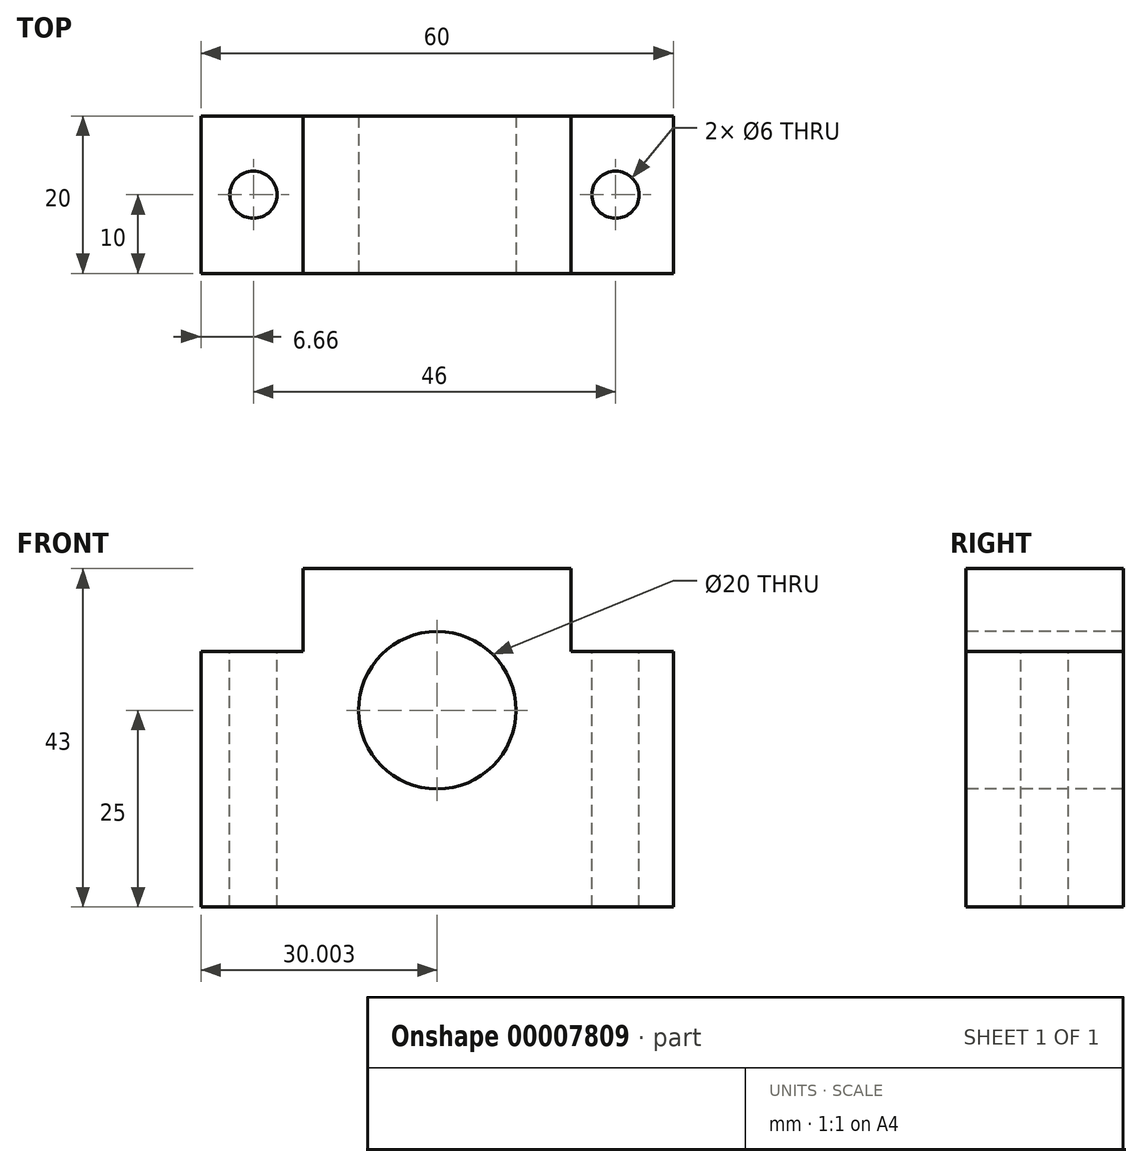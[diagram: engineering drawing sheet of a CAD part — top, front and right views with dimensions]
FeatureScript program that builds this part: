
annotation { "Feature Type Name" : "Feature", "Feature Type Description" : "" }
export const myFeature = defineFeature(function(context is Context, id is Id, definition is map)
    precondition{}
    {
        {
            var Q0;
            Q0=qCreatedBy(makeId("Front.planeOp"),FACE);
            var sketch = newSketch(context, id + "F0", { "sketchPlane" : qUnion([Q0])});
            skLineSegment(sketch, "E0.bottom", {"start": v(-29.66, 0) * mm, "end": v(30.34, 0) * mm});
            skLineSegment(sketch, "E0.top", {"start": v(-29.66, 32.5) * mm, "end": v(-16.66, 32.5) * mm});
            skLineSegment(sketch, "E0.left", {"start": v(-29.66, 0) * mm, "end": v(-29.66, 32.5) * mm});
            skLineSegment(sketch, "E0.right", {"start": v(30.34, 0) * mm, "end": v(30.34, 32.5) * mm});
            skLineSegment(sketch, "E1.top", {"start": v(-16.66, 43) * mm, "end": v(17.34, 43) * mm});
            skLineSegment(sketch, "E1.left", {"start": v(-16.66, 32.5) * mm, "end": v(-16.66, 43) * mm});
            skLineSegment(sketch, "E1.right", {"start": v(17.34, 32.5) * mm, "end": v(17.34, 43) * mm});
            skLineSegment(sketch, "E2.trimOffspring", {"start": v(17.34, 32.5) * mm, "end": v(30.34, 32.5) * mm});
            skSolve(sketch);
        }
        {
            var Q0;
            Q0=qSketchRegion(id+"F0",true);
            extrude(context, id + "F1", {"entities" : qUnion([Q0]), "oppositeDirection" : true, "depth" : 20 * mm});
        }
        {
            var Q0;
            Q0=makeQuery(id+"F1.opExtrude","SWEPT_FACE",FACE,{"disambiguationData":[OSD([sQuery(id+"F0.wireOp",EDGE,"E2.trimOffspring")])]});
            var sketch = newSketch(context, id + "F2", { "sketchPlane" : qUnion([Q0])});
            skCircle(sketch, "E3", {"center": v(23, 10) * mm, "radius": 3 * mm});
            skLineSegment(sketch, "E4", {"start": v(0, 0) * mm, "end": v(0, 23.2) * mm});
            skCircle(sketch, "E5.0.MirrorC", {"center": v(-23, 10) * mm, "radius": 3 * mm});
            skSolve(sketch);
        }
        {
            var Q0;
            Q0 = qSketchRegion(id + "F2", true);
            extrude(context, id + "F3", {"entities" : qUnion([Q0]), "operationType" : NewBodyOperationType.REMOVE, "endBound" : BoundingType.THROUGH_ALL, "oppositeDirection" : true, "depth" : 25 * mm});
        }
        {
            var Q0;
            Q0=makeQuery(id+"F1.opExtrude","CAP_FACE",FACE,{"disambiguationData":[OSD([sQuery(id+"F0.wireOp",EDGE,"E0.bottom"),sQuery(id+"F0.wireOp",EDGE,"E0.top"),sQuery(id+"F0.wireOp",EDGE,"E0.left"),sQuery(id+"F0.wireOp",EDGE,"E0.right"),sQuery(id+"F0.wireOp",EDGE,"E1.top"),sQuery(id+"F0.wireOp",EDGE,"E1.left"),sQuery(id+"F0.wireOp",EDGE,"E1.right"),sQuery(id+"F0.wireOp",EDGE,"E2.trimOffspring")])],"isStart":true});
            var sketch = newSketch(context, id + "F4", { "sketchPlane" : qUnion([Q0])});
            skCircle(sketch, "E6", {"center": v(0.34, 25) * mm, "radius": 10 * mm});
            skSolve(sketch);
        }
        {
            var Q0;
            Q0 = qSketchRegion(id + "F4", true);
            extrude(context, id + "F5", {"entities" : qUnion([Q0]), "operationType" : NewBodyOperationType.REMOVE, "endBound" : BoundingType.THROUGH_ALL, "oppositeDirection" : true, "depth" : 25 * mm});
        }
    });
